# Revit family: Loudspeaker-Ceiling Mounted-Q-SYS-AD-C8T-SWZB-Subwoofer
name_source: partatom
category: Communication Devices
units: mm (PartAtom-declared; Revit-internal decimal feet)

## family parameters
Cut with Voids When Loaded = No
Host = Face
Maintain Annotation Orientation = No
OmniClass Number = 23.85.10.11.14.14.14
OmniClass Title = Loudspeakers
Part Type = Normal
Room Calculation Point = No
Round Connector Dimension = Use Diameter
Shared = No

## types (1)
- White
    100V Taps = 50 W, 100 W, 200 W
    70V Taps = 25 W, 50 W, 100 W, 200 W
    ATB Inside Diameter = 12 "
    ATB Inside Radius = 6 "
    Assembly Code = E1020300
    Body Diameter = 11.4 "
    Body Height = 13.37 "
    Body Material = Paint - Q-SYS - Black
    Body Radius = 5.7 "
    Clip Diameter = 0.3 "
    Clip Height = 0.45 "
    Clip Radius = 0.15 "
    Cover Diameter = 11.5 "
    Cover Material = Paint - Q-SYS - White
    Cover Radius = 5.75 "
    Coverage Horizontal = 90.00°
    Coverage Vertical = 90.00°
    Default Elevation = 48 "
    Description = 8” zero bezel ceiling mount subwoofer loudspeaker.
    Frequency Range = 53 Hz - 195 Hz
    Grille Diameter = 13.23 "
    Grille Height = 0.158 "
    Grille Radius = 6.615 "
    Highlight Material = Fabric - Q-SYS - White Mesh
    IQ Category = Loudspeaker
    Impedance = 6.4
    Length 1 = 5.45 "
    Length 10 = 0.999 "
    Length 11 = 0.575 "
    Length 15 = 5.75 "
    Length 2 = 2.75 "
    Length 4 = 6.8 "
    Length 7 = 1 "
    Length 8 = 0.768 "
    Length 9 = 0.595 "
    Manufacturer = Q-SYS
    Manufacturer URL = https://www.qsys.com
    Model = AD-C8T-SWZB
    Number of Bands = 1
    Offset = 0 "
    OmniClass Number = 23.85.10.11.14.14.14
    Part Number = AD-C8T-SWZB
    Product Documentation Link = https://www.qsys.com
    Product Page URL = https://www.qsys.com
    Rail Width = 0.875 "
    Regulatory Compliance = ROHS, CE
    SPL Max = 113
    Sensitivity = 92.3
    Support Length = 25.57 "
    Support Material = Metal - Q-SYS - Steel
    Support Width = 25.3 "
    Taper Angle = 3.00°
    Type Comments = White
    URL = https://www.qsys.com
    Unit Size = 16.2
    Weight = 22.40 lbm
    Weight Dimensional = 66.9
    Weight Product = 22.4
    Width = 13.23 "

## geometry (parser evidence)
native form markers: Blend x2, Sweep x5
no freeform markers — native parametric forms only
